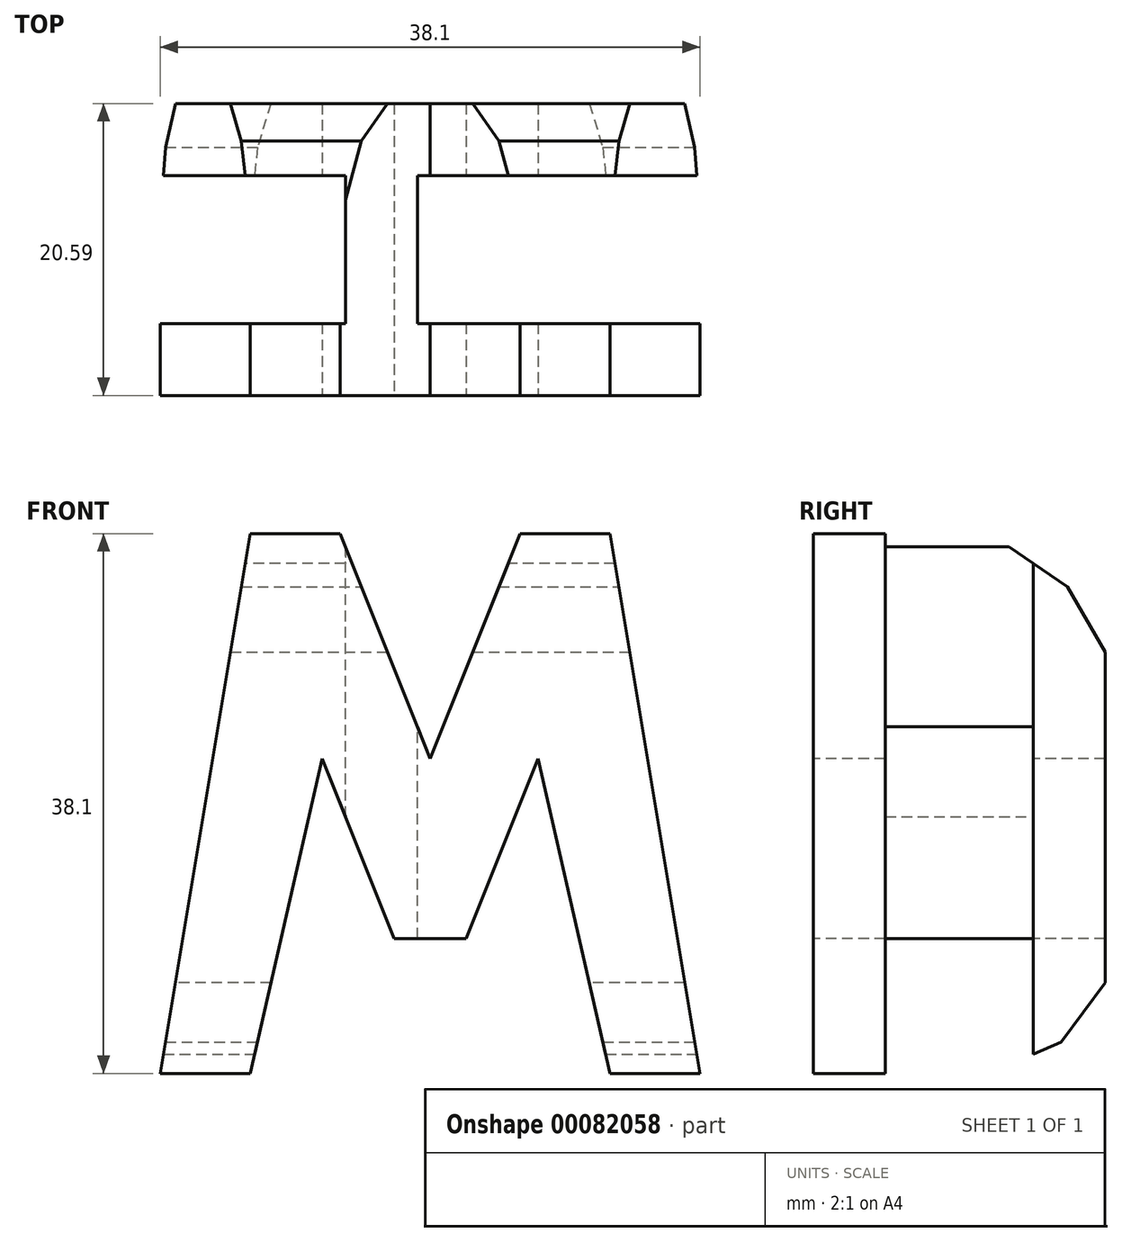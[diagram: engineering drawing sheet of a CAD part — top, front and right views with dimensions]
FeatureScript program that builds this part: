
annotation { "Feature Type Name" : "Feature", "Feature Type Description" : "" }
export const myFeature = defineFeature(function(context is Context, id is Id, definition is map)
    precondition{}
    {
        {
            var Q0;
            Q0=qCreatedBy(makeId("Front.planeOp"),FACE);
            var sketch = newSketch(context, id + "F0", { "sketchPlane" : qUnion([Q0])});
            skLineSegment(sketch, "E0.bottom", {"start": v(0, 0) * mm, "end": v(38.1, 0) * mm});
            skLineSegment(sketch, "E0.top", {"start": v(0, 38.1) * mm, "end": v(38.1, 38.1) * mm});
            skLineSegment(sketch, "E0.left", {"start": v(0, 0) * mm, "end": v(0, 38.1) * mm});
            skLineSegment(sketch, "E0.right", {"start": v(38.1, 0) * mm, "end": v(38.1, 38.1) * mm});
            skSolve(sketch);
        }
        {
            var Q0;
            Q0 = qSketchRegion(id + "F0", true);
            extrude(context, id + "F1", {"entities" : qUnion([Q0]), "depth" : 38.1 * mm});
        }
        {
            var Q0;
            Q0=qCreatedBy(makeId("Front.planeOp"),FACE);
            cPlane(context, id + "F2", {"entities" : qUnion([Q0]), "cplaneType" : CPlaneType.OFFSET, "offset" : 38.1 * mm, "width" : 152.4 * mm, "height" : 152.4 * mm});
        }
        {
            var Q0;
            Q0=qCreatedBy(makeId("Right.planeOp"),FACE);
            cPlane(context, id + "F3", {"entities" : qUnion([Q0]), "cplaneType" : CPlaneType.OFFSET, "offset" : 38.1 * mm, "width" : 152.4 * mm, "height" : 152.4 * mm});
        }
        {
            var Q0;
            Q0=qCreatedBy(makeId("Top.planeOp"),FACE);
            cPlane(context, id + "F4", {"entities" : qUnion([Q0]), "cplaneType" : CPlaneType.OFFSET, "offset" : 38.1 * mm, "width" : 152.4 * mm, "height" : 152.4 * mm});
        }
        {
            var Q0;
            Q0=qCreatedBy(id+"F2.planeOp",FACE);
            var sketch = newSketch(context, id + "F5", { "sketchPlane" : qUnion([Q0])});
            skLineSegment(sketch, "E1.bottom", {"start": v(0, 0) * mm, "end": v(38.1, 0) * mm});
            skLineSegment(sketch, "E1.top", {"start": v(0, 38.1) * mm, "end": v(38.1, 38.1) * mm});
            skLineSegment(sketch, "E1.left", {"start": v(0, 0) * mm, "end": v(0, 38.1) * mm});
            skLineSegment(sketch, "E1.right", {"start": v(38.1, 0) * mm, "end": v(38.1, 38.1) * mm});
            skLineSegment(sketch, "E2", {"start": v(0, 0) * mm, "end": v(6.35, 38.1) * mm});
            skLineSegment(sketch, "E3", {"start": v(6.35, 38.1) * mm, "end": v(12.7, 38.1) * mm});
            skLineSegment(sketch, "E4", {"start": v(12.7, 38.1) * mm, "end": v(19.05, 22.22) * mm});
            skLineSegment(sketch, "E5", {"start": v(19.05, 22.23) * mm, "end": v(25.4, 38.1) * mm});
            skLineSegment(sketch, "E6", {"start": v(25.4, 38.1) * mm, "end": v(31.75, 38.1) * mm});
            skLineSegment(sketch, "E7", {"start": v(31.75, 38.1) * mm, "end": v(38.1, 0) * mm});
            skLineSegment(sketch, "E8", {"start": v(16.51, 9.53) * mm, "end": v(21.59, 9.53) * mm});
            skLineSegment(sketch, "E9", {"start": v(21.59, 9.52) * mm, "end": v(26.67, 22.23) * mm});
            skLineSegment(sketch, "E10", {"start": v(26.67, 22.23) * mm, "end": v(31.75, 0) * mm});
            skLineSegment(sketch, "E11", {"start": v(16.51, 9.52) * mm, "end": v(11.43, 22.22) * mm});
            skLineSegment(sketch, "E12", {"start": v(11.43, 22.22) * mm, "end": v(6.35, 0) * mm});
            skSolve(sketch);
        }
        {
            var Q0;
            {var subQ0=sQuery(id+"F5.wireOp",EDGE,"E1.left");Q0=makeQuery(id+"F5.imprint","IMPRINT",FACE,{"disambiguationData":[TD([[makeQuery(id+"F5.imprint","IMPRINT",EDGE,{"derivedFrom":subQ0}),-1.0]])]});}
            var Q1;
            {var subQ0=sQuery(id+"F5.wireOp",EDGE,"E4");Q1=makeQuery(id+"F5.imprint","IMPRINT",FACE,{"disambiguationData":[TD([[makeQuery(id+"F5.imprint","IMPRINT",EDGE,{"derivedFrom":subQ0}),1.0]])]});}
            var Q2;
            {var subQ0=sQuery(id+"F5.wireOp",EDGE,"E1.right");Q2=makeQuery(id+"F5.imprint","IMPRINT",FACE,{"disambiguationData":[TD([[makeQuery(id+"F5.imprint","IMPRINT",EDGE,{"derivedFrom":subQ0}),1.0]])]});}
            var Q3;
            Q3=makeQuery(id+"F5.imprint","IMPRINT",FACE,{"disambiguationData":[TD([[makeQuery(id+"F5.imprint","IMPRINT",EDGE,{"derivedFrom":sQuery(id+"F5.wireOp",EDGE,"E8")}),-1.0]])]});
            extrude(context, id + "F6", {"entities" : qUnion([Q0, Q1, Q2, Q3]), "operationType" : NewBodyOperationType.REMOVE, "oppositeDirection" : true, "depth" : 38.1 * mm});
        }
        {
            var Q0;
            Q0=qCreatedBy(id+"F3.planeOp",FACE);
            var sketch = newSketch(context, id + "F7", { "sketchPlane" : qUnion([Q0])});
            skLineSegment(sketch, "E13.bottom", {"start": v(0, 0) * mm, "end": v(-38.1, 0) * mm});
            skLineSegment(sketch, "E13.top", {"start": v(0, 38.1) * mm, "end": v(-38.1, 38.1) * mm});
            skLineSegment(sketch, "E13.left", {"start": v(0, 0) * mm, "end": v(0, 38.1) * mm});
            skLineSegment(sketch, "E13.right", {"start": v(-38.1, 0) * mm, "end": v(-38.1, 38.1) * mm});
            skLineSegment(sketch, "E14", {"start": v(-33.25, 0) * mm, "end": v(-33.25, 38.1) * mm});
            skLineSegment(sketch, "E15", {"start": v(-33.25, 38.1) * mm, "end": v(-19.05, 38.1) * mm});
            skLineSegment(sketch, "E16", {"start": v(-19.05, 38.1) * mm, "end": v(-33.25, 38.1) * mm});
            skLineSegment(sketch, "E17", {"start": v(-33.25, 0) * mm, "end": v(-19.05, 0) * mm});
            skLineSegment(sketch, "E18", {"start": v(-19.05, 0) * mm, "end": v(-13.96, 2.22) * mm});
            skLineSegment(sketch, "E19", {"start": v(-13.96, 2.22) * mm, "end": v(-10.86, 6.43) * mm});
            skLineSegment(sketch, "E20", {"start": v(-10.86, 6.43) * mm, "end": v(-10.86, 13.08) * mm});
            skLineSegment(sketch, "E21", {"start": v(-10.86, 13.08) * mm, "end": v(-10.86, 19.73) * mm});
            skLineSegment(sketch, "E22", {"start": v(-10.86, 19.73) * mm, "end": v(-10.86, 29.7) * mm});
            skLineSegment(sketch, "E23", {"start": v(-10.86, 29.7) * mm, "end": v(-13.52, 34.35) * mm});
            skLineSegment(sketch, "E24", {"start": v(-13.52, 34.35) * mm, "end": v(-19.05, 38.1) * mm});
            skLineSegment(sketch, "E25", {"start": v(-19.05, 0) * mm, "end": v(-33.25, 0) * mm});
            skSolve(sketch);
        }
        {
            var Q0;
            {var subQ0=sQuery(id+"F7.wireOp",EDGE,"E13.right");Q0=makeQuery(id+"F7.imprint","IMPRINT",FACE,{"disambiguationData":[TD([[makeQuery(id+"F7.imprint","IMPRINT",EDGE,{"derivedFrom":subQ0}),-1.0]])]});}
            var Q1;
            {var subQ0=sQuery(id+"F7.wireOp",EDGE,"E13.left");Q1=makeQuery(id+"F7.imprint","IMPRINT",FACE,{"disambiguationData":[TD([[makeQuery(id+"F7.imprint","IMPRINT",EDGE,{"derivedFrom":subQ0}),1.0]])]});}
            extrude(context, id + "F8", {"entities" : qUnion([Q0, Q1]), "operationType" : NewBodyOperationType.REMOVE, "oppositeDirection" : true, "depth" : 38.1 * mm});
        }
        {
            var Q0;
            Q0=qCreatedBy(id+"F4.planeOp",FACE);
            var sketch = newSketch(context, id + "F9", { "sketchPlane" : qUnion([Q0])});
            skLineSegment(sketch, "E26.bottom", {"start": v(0, 0) * mm, "end": v(38.1, 0) * mm});
            skLineSegment(sketch, "E26.top", {"start": v(0, -38.1) * mm, "end": v(38.1, -38.1) * mm});
            skLineSegment(sketch, "E26.left", {"start": v(0, 0) * mm, "end": v(0, -38.1) * mm});
            skLineSegment(sketch, "E26.right", {"start": v(38.1, 0) * mm, "end": v(38.1, -38.1) * mm});
            skLineSegment(sketch, "E27", {"start": v(0, -10.88) * mm, "end": v(38.1, -10.88) * mm});
            skLineSegment(sketch, "E28", {"start": v(38.1, -10.88) * mm, "end": v(38.1, -15.96) * mm});
            skLineSegment(sketch, "E29", {"start": v(38.1, -15.96) * mm, "end": v(18.16, -15.96) * mm});
            skLineSegment(sketch, "E30", {"start": v(18.16, -15.96) * mm, "end": v(18.16, -26.4) * mm});
            skLineSegment(sketch, "E31", {"start": v(18.16, -26.4) * mm, "end": v(38.1, -26.4) * mm});
            skLineSegment(sketch, "E32", {"start": v(38.1, -26.4) * mm, "end": v(38.1, -31.47) * mm});
            skLineSegment(sketch, "E33", {"start": v(38.1, -31.47) * mm, "end": v(0, -31.47) * mm});
            skLineSegment(sketch, "E34", {"start": v(0, -31.47) * mm, "end": v(0, -26.4) * mm});
            skLineSegment(sketch, "E35", {"start": v(0, -26.4) * mm, "end": v(13.08, -26.4) * mm});
            skLineSegment(sketch, "E36", {"start": v(13.08, -26.4) * mm, "end": v(13.08, -15.96) * mm});
            skLineSegment(sketch, "E37", {"start": v(13.08, -15.96) * mm, "end": v(0, -15.96) * mm});
            skLineSegment(sketch, "E38", {"start": v(0, -15.96) * mm, "end": v(0, -10.88) * mm});
            skSolve(sketch);
        }
        {
            var Q0;
            {var subQ0=sQuery(id+"F9.wireOp",EDGE,"E29");Q0=makeQuery(id+"F9.imprint","IMPRINT",FACE,{"disambiguationData":[TD([[makeQuery(id+"F9.imprint","IMPRINT",EDGE,{"derivedFrom":subQ0}),1.0]])]});}
            var Q1;
            {var subQ0=sQuery(id+"F9.wireOp",EDGE,"E35");Q1=makeQuery(id+"F9.imprint","IMPRINT",FACE,{"disambiguationData":[TD([[makeQuery(id+"F9.imprint","IMPRINT",EDGE,{"derivedFrom":subQ0}),1.0]])]});}
            var Q2;
            {var subQ0=sQuery(id+"F9.wireOp",EDGE,"E26.top");Q2=makeQuery(id+"F9.imprint","IMPRINT",FACE,{"disambiguationData":[TD([[makeQuery(id+"F9.imprint","IMPRINT",EDGE,{"derivedFrom":subQ0}),1.0]])]});}
            var Q3;
            {var subQ0=sQuery(id+"F9.wireOp",EDGE,"E26.bottom");Q3=makeQuery(id+"F9.imprint","IMPRINT",FACE,{"disambiguationData":[TD([[makeQuery(id+"F9.imprint","IMPRINT",EDGE,{"derivedFrom":subQ0}),-1.0]])]});}
            extrude(context, id + "F10", {"entities" : qUnion([Q0, Q1, Q2, Q3]), "operationType" : NewBodyOperationType.REMOVE, "oppositeDirection" : true, "depth" : 38.1 * mm});
        }
    });
